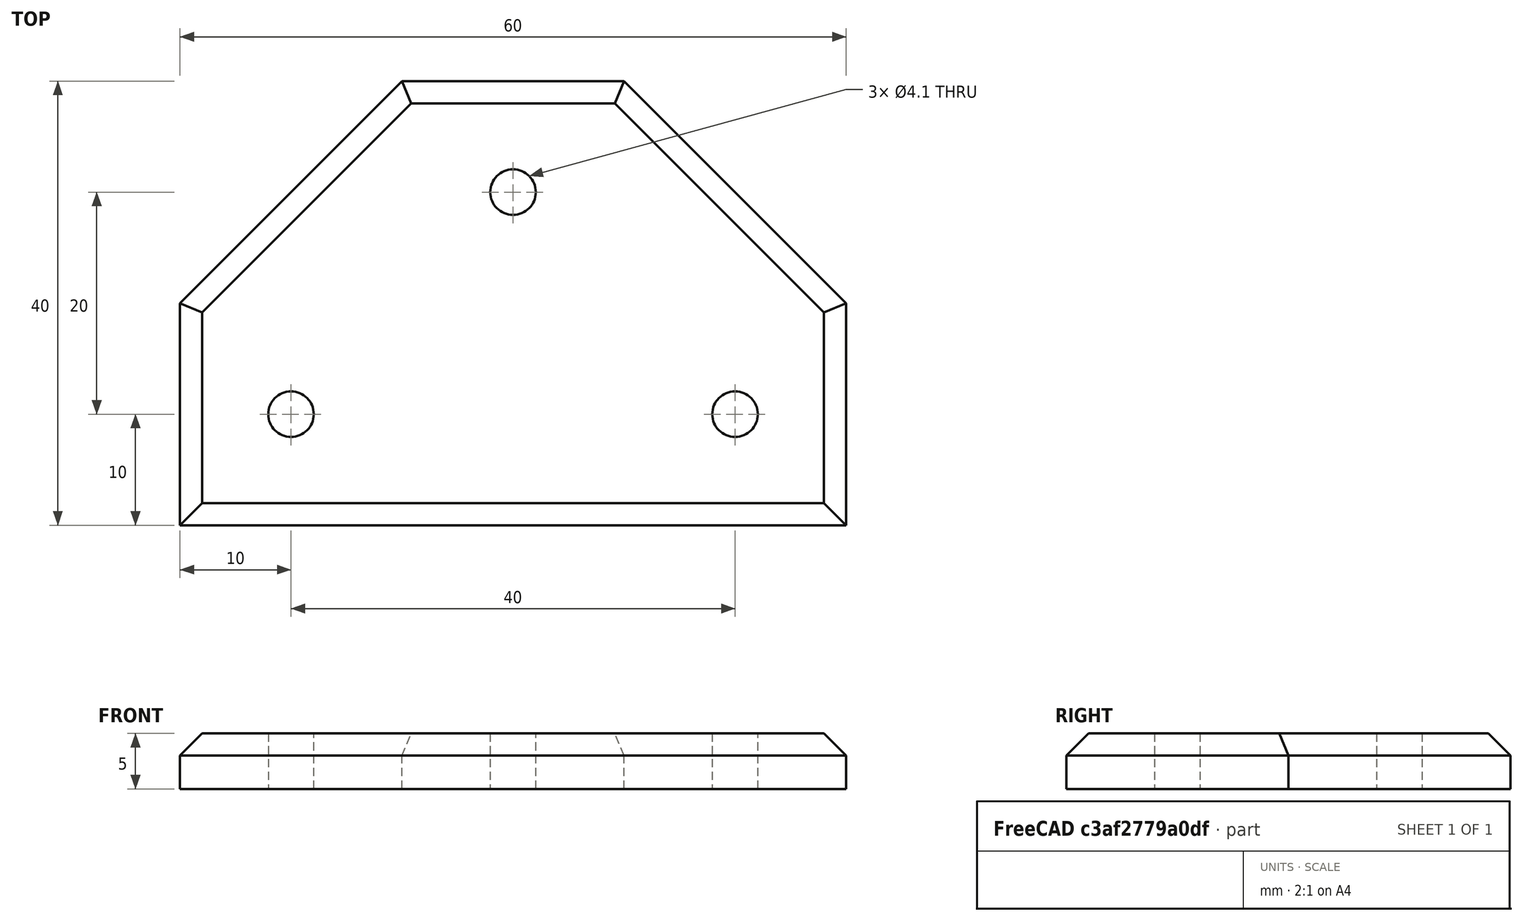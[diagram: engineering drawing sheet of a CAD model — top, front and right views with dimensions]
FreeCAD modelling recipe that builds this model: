
FCSTD DOCUMENT  (FreeCAD 0.14R3702 (Git))
Label: TTrapBracked]t
License: CC-BY 3.0
LicenseURL: http://creativecommons.org/licenses/by/3.0/
objects: Sketcher::SketchObject×2, Part::Extrusion×1, Part::Chamfer×1
note: 4 computed .brp shape members not serialized (recipe doc carries the construction recipe); baked Part::Feature solids carry a one-line shape summary decoded from their .brp

FEATURE [Sketcher::SketchObject] Sketch
  sketch-geometry (9):
    g0: LineSegment StartX=0 StartY=0 StartZ=0 EndX=0 EndY=20 EndZ=0
    g1: LineSegment StartX=20 StartY=40 StartZ=0 EndX=40 EndY=40 EndZ=0
    g2: LineSegment StartX=60 StartY=20 StartZ=0 EndX=60 EndY=0 EndZ=0
    g3: LineSegment StartX=60 StartY=0 StartZ=0 EndX=0 EndY=0 EndZ=0
    g4: Circle CenterX=10 CenterY=10 CenterZ=0 NormalX=0 NormalY=0 NormalZ=1 Radius=2.05
    g5: Circle CenterX=50 CenterY=10 CenterZ=0 NormalX=0 NormalY=0 NormalZ=1 Radius=2.05
    g6: Circle CenterX=30 CenterY=30 CenterZ=0 NormalX=0 NormalY=0 NormalZ=1 Radius=2.05
    g7: LineSegment StartX=0 StartY=20 StartZ=0 EndX=20 EndY=40 EndZ=0
    g8: LineSegment StartX=40 StartY=40 StartZ=0 EndX=60 EndY=20 EndZ=0
  constraints (13):
    c: PointOnObject(g0,g-2)
    c: Vertical(g0)
    c: Horizontal(g1)
    c: DistanceX(g1) = 20
    c: PointOnObject(g2,g-1)
    c: Vertical(g2)
    c: PointOnObject(g3,g-1)
    c: PointOnObject(g3,g-2)
    c: Horizontal(g3)
    c: PointOnObject(g7,g0)
    c: Radius(g4) = 2.05
    c: Equal(g4,g5)
    c: Equal(g5,g6)
FEATURE [Part::Extrusion] Extrude
  Base = -> Sketch
  Dir = (0,0,5)
  Solid = true
FEATURE [Part::Chamfer] Chamfer
  Base = -> Extrude
  Edges = 6 edges r=2: [Edge4,Edge7,Edge10,Edge13,Edge16,Edge18]
FEATURE [Sketcher::SketchObject] Sketch001
  sketch-geometry (1):
    g0: LineSegment [constr] StartX=10 StartY=10 StartZ=0 EndX=50 EndY=10 EndZ=0
  constraints (1):
    c: Horizontal(g0)
